# Revit family: BIM_Model_Piranhamat_ 1002_50_D01
name_source: partatom
category: Mechanical Equipment
revit_build: Autodesk Revit 2018 (Build: 20170223_1515(x64)
units: mm (PartAtom-declared; Revit-internal decimal feet)

## family parameters
Always vertical = Yes
Cut with Voids When Loaded = No
Part Type = Normal
Room Calculation Point = No
Round Connector Dimension = Use Radius
Shared = No
Work Plane-Based = No

## types (1)
- Piranhamat 1002 D
    Bottom Plate = Cast Iron EN-GJL-250
    Cable Length (m) = 4.0
    Cable Type (S1BN8-F) = 4G1.5
    Capacity(m3/hr) = 9 m³
    Description = Flood-proof, double lifting station, for automatic sewage pumping
from areas below the backwash level in accordance with
EN 12050-1. The Piranhamat 1002 is used for reliable and
economical discharge of wastewater under pressure using small
diameter discharge lines. Suitable for new installations or for
renovation of old buildings.
pumping from areas below the backwash level in accordance
with EN 12050-1. The Piranhamat 1002 is used for reliable and
economical discharge of wastewater under pressure using
small diameter discharge lines. Suitable for new installations
or for renovation of old buildings.
    Discharge DN32 = 16 mm  [stored 0.0524934 ft]
    Discharge line DN 32 (with ball valve) = 16 mm  [stored 0.0524934 ft]
    Fasteners = Stainless steel 1.4401 (AISI 316)
    Head(m) = 30 mm  [stored 0.0984252 ft]
    Impeller = Cast Iron EN-GJL-250
    Inflow / Vent DN 100 = 50 mm  [stored 0.164042 ft]
    Inflow / Vent DN 70 = 35 mm  [stored 0.114829 ft]
    Inflow DN 100 = 50 mm  [stored 0.164042 ft]
    Inflow DN 150 = 75 mm
    Inflow DN 50 = 25 mm  [stored 0.082021 ft]
    Inflow/Hand Membrane Pump DN 40 = 20 mm  [stored 0.0656168 ft]
    Manufacturer = Sulzer
    Model = Lifting Station Type ABS Piranhamat 1002
    Motor Housing = Cast Iron EN-GJL-250
    Motor Power (kW) = P1=2.3 P2=1.7
    Product Specification Link = https://www.sulzer.com
    Rated Current (A) = 4.0
    Rated Voltage (V) = 400 3~
    Rotor Shaft = Stainless steel 1.4021 (AISI 420)
    Speed (r/min) = 2900
    Tank Material = Polyethylene
    Volute = Cast Iron EN-GJL-250
    Weight (Kg) = 98

note: [stored X ft] marks values corroborated as IEEE doubles in the binary element streams (Revit-internal decimal feet)

## geometry (parser evidence)
native form markers: Sweep x3
no freeform markers — native parametric forms only
